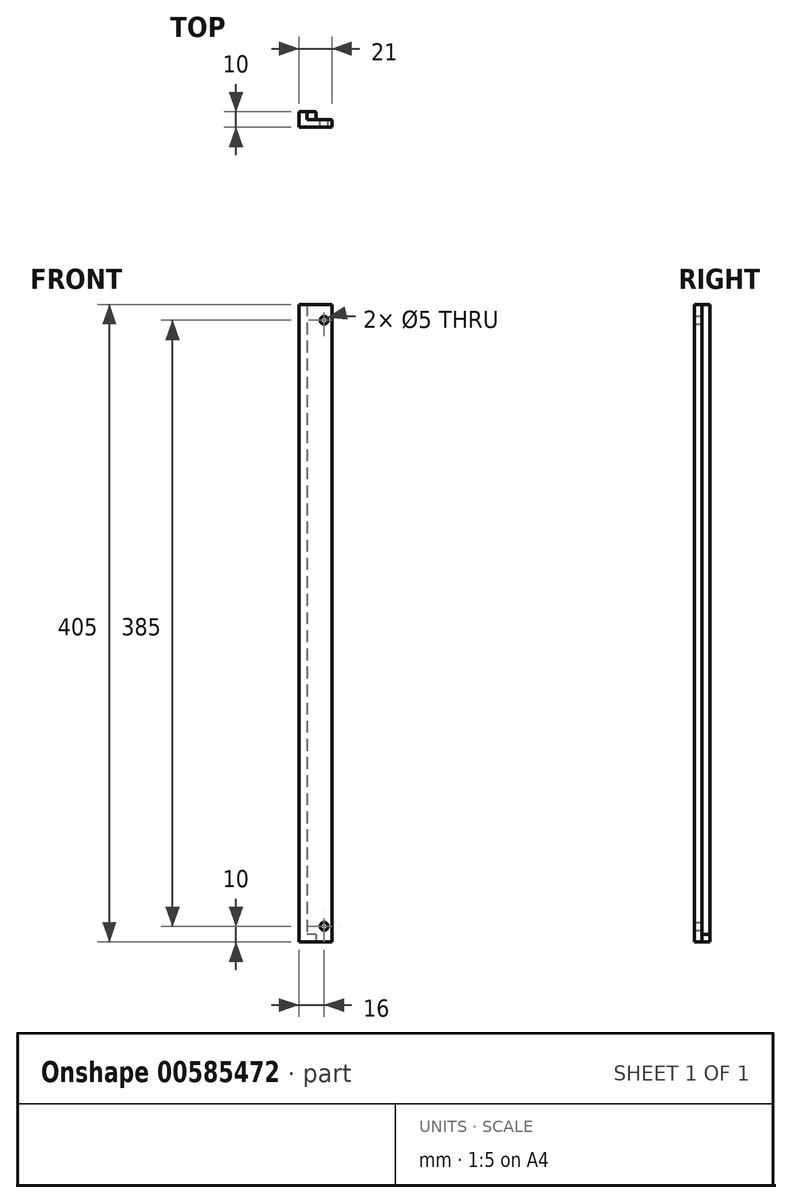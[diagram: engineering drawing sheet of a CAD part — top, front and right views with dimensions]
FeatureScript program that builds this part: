
annotation { "Feature Type Name" : "Feature", "Feature Type Description" : "" }
export const myFeature = defineFeature(function(context is Context, id is Id, definition is map)
    precondition{}
    {
        {
            var Q0;
            Q0=qCreatedBy(makeId("Top.planeOp"),FACE);
            var sketch = newSketch(context, id + "F0", { "sketchPlane" : qUnion([Q0])});
            skLineSegment(sketch, "E0", {"start": v(0, 0) * mm, "end": v(0, -10) * mm});
            skLineSegment(sketch, "E1", {"start": v(0, -10) * mm, "end": v(21, -10) * mm});
            skLineSegment(sketch, "E2", {"start": v(21, -10) * mm, "end": v(21, -5) * mm});
            skLineSegment(sketch, "E3", {"start": v(21, -5) * mm, "end": v(11, -5) * mm});
            skLineSegment(sketch, "E4", {"start": v(11, -5) * mm, "end": v(11, 0) * mm});
            skLineSegment(sketch, "E5", {"start": v(11, 0) * mm, "end": v(6, 0) * mm});
            skLineSegment(sketch, "E6", {"start": v(5, 0) * mm, "end": v(0, 0) * mm});
            skLineSegment(sketch, "E7", {"start": v(5, 0) * mm, "end": v(6, 0) * mm});
            skSolve(sketch);
        }
        {
            var Q0;
            Q0=makeQuery(id+"F0.imprint","IMPRINT",FACE,{"disambiguationData":[TD([[makeQuery(id+"F0.imprint","IMPRINT",EDGE,{"derivedFrom":sQuery(id+"F0.wireOp",EDGE,"E0")}),1.0]])]});
            extrude(context, id + "F1", {"entities" : qUnion([Q0]), "depth" : 5 * mm, "offsetDistance" : 25 * mm});
        }
        {
            var Q0;
            Q0=makeQuery(id+"F1.opExtrude","CAP_FACE",FACE,{"disambiguationData":[OSD([sQuery(id+"F0.wireOp",EDGE,"E0"),sQuery(id+"F0.wireOp",EDGE,"E1"),sQuery(id+"F0.wireOp",EDGE,"E2"),sQuery(id+"F0.wireOp",EDGE,"E3"),sQuery(id+"F0.wireOp",EDGE,"E4"),sQuery(id+"F0.wireOp",EDGE,"E5"),sQuery(id+"F0.wireOp",EDGE,"E6"),sQuery(id+"F0.wireOp",EDGE,"E7")])],"isStart":false});
            var sketch = newSketch(context, id + "F2", { "sketchPlane" : qUnion([Q0])});
            skLineSegment(sketch, "E8", {"start": v(0, 0) * mm, "end": v(0, -10) * mm});
            skLineSegment(sketch, "E9", {"start": v(0, -10) * mm, "end": v(21, -10) * mm});
            skLineSegment(sketch, "E10", {"start": v(21, -10) * mm, "end": v(21, -5) * mm});
            skLineSegment(sketch, "E11", {"start": v(21, -5) * mm, "end": v(11, -5) * mm});
            skLineSegment(sketch, "E12", {"start": v(11, -5) * mm, "end": v(11, 0) * mm});
            skLineSegment(sketch, "E13", {"start": v(11, 0) * mm, "end": v(6, 0) * mm});
            skLineSegment(sketch, "E14", {"start": v(6, 0) * mm, "end": v(6, -5) * mm});
            skLineSegment(sketch, "E15", {"start": v(6, -5) * mm, "end": v(5, -5) * mm});
            skLineSegment(sketch, "E16", {"start": v(5, -5) * mm, "end": v(5, 0) * mm});
            skLineSegment(sketch, "E17", {"start": v(5, 0) * mm, "end": v(0, 0) * mm});
            skSolve(sketch);
        }
        {
            var Q0;
            Q0=makeQuery(id+"F2.imprint","IMPRINT",FACE,{"disambiguationData":[TD([[makeQuery(id+"F2.imprint","IMPRINT",EDGE,{"derivedFrom":sQuery(id+"F2.wireOp",EDGE,"E8")}),1.0]])]});
            extrude(context, id + "F3", {"entities" : qUnion([Q0]), "operationType" : NewBodyOperationType.ADD, "depth" : 400 * mm, "offsetDistance" : 25 * mm});
        }
        {
            var Q0;
            Q0=makeQuery(id+"F3.boolean.opBoolean","MERGE",FACE,{"derivedFrom":[makeQuery(id+"F1.opExtrude","SWEPT_FACE",FACE,{"disambiguationData":[OSD([sQuery(id+"F0.wireOp",EDGE,"E3")])]}),makeQuery(id+"F3.opExtrude","SWEPT_FACE",FACE,{"disambiguationData":[OSD([sQuery(id+"F2.wireOp",EDGE,"E11")])]})]});
            var sketch = newSketch(context, id + "F4", { "sketchPlane" : qUnion([Q0])});
            skLineSegment(sketch, "E18", {"start": v(-16, 0) * mm, "end": v(-16, 10) * mm});
            skSolve(sketch);
        }
        {
            var Q0;
            Q0=sQuery(id+"F4.wireOp",VERTEX,"E18.end");
            var Q1;
            Q1=makeQuery(id+"F1.opExtrude","SWEPT_BODY",BODY,{"disambiguationData":[OSD([sQuery(id+"F0.wireOp",EDGE,"E0"),sQuery(id+"F0.wireOp",EDGE,"E1"),sQuery(id+"F0.wireOp",EDGE,"E2"),sQuery(id+"F0.wireOp",EDGE,"E3"),sQuery(id+"F0.wireOp",EDGE,"E4"),sQuery(id+"F0.wireOp",EDGE,"E5"),sQuery(id+"F0.wireOp",EDGE,"E6"),sQuery(id+"F0.wireOp",EDGE,"E7")])]});
            hole(context, id + "F5", {"style" : HoleStyle.SIMPLE, "endStyle" : HoleEndStyle.THROUGH, "holeDiameter" : 5 * mm, "majorDiameter" : 5 * mm, "isTappedThrough" : true, "tappedDepth" : 12 * mm, "tapClearance" : 3, "locations" : qUnion([Q0]), "scope" : qUnion([Q1])});
        }
        {
            var Q0;
            Q0=makeQuery(id+"F3.boolean.opBoolean","MERGE",FACE,{"derivedFrom":[makeQuery(id+"F1.opExtrude","SWEPT_FACE",FACE,{"disambiguationData":[OSD([sQuery(id+"F0.wireOp",EDGE,"E3")])]}),makeQuery(id+"F3.opExtrude","SWEPT_FACE",FACE,{"disambiguationData":[OSD([sQuery(id+"F2.wireOp",EDGE,"E11")])]})]});
            var sketch = newSketch(context, id + "F6", { "sketchPlane" : qUnion([Q0])});
            skLineSegment(sketch, "E19", {"start": v(-16, 405) * mm, "end": v(-16, 395) * mm});
            skPoint(sketch, "E19.endSnap0", {"position": v(-16, 405) * mm});
            skSolve(sketch);
        }
        {
            var Q0;
            Q0=sQuery(id+"F6.wireOp",VERTEX,"E19.end");
            var Q1;
            Q1=makeQuery(id+"F1.opExtrude","SWEPT_BODY",BODY,{"disambiguationData":[OSD([sQuery(id+"F0.wireOp",EDGE,"E0"),sQuery(id+"F0.wireOp",EDGE,"E1"),sQuery(id+"F0.wireOp",EDGE,"E2"),sQuery(id+"F0.wireOp",EDGE,"E3"),sQuery(id+"F0.wireOp",EDGE,"E4"),sQuery(id+"F0.wireOp",EDGE,"E5"),sQuery(id+"F0.wireOp",EDGE,"E6"),sQuery(id+"F0.wireOp",EDGE,"E7")])]});
            hole(context, id + "F7", {"style" : HoleStyle.SIMPLE, "endStyle" : HoleEndStyle.THROUGH, "holeDiameter" : 5 * mm, "majorDiameter" : 5 * mm, "isTappedThrough" : true, "tappedDepth" : 12 * mm, "tapClearance" : 3, "locations" : qUnion([Q0]), "scope" : qUnion([Q1])});
        }
        {
            var Q0;
            Q0=makeQuery(id+"F3.opExtrude","CAP_FACE",FACE,{"disambiguationData":[OSD([sQuery(id+"F2.wireOp",EDGE,"E8"),sQuery(id+"F2.wireOp",EDGE,"E9"),sQuery(id+"F2.wireOp",EDGE,"E10"),sQuery(id+"F2.wireOp",EDGE,"E11"),sQuery(id+"F2.wireOp",EDGE,"E12"),sQuery(id+"F2.wireOp",EDGE,"E13"),sQuery(id+"F2.wireOp",EDGE,"E14"),sQuery(id+"F2.wireOp",EDGE,"E15"),sQuery(id+"F2.wireOp",EDGE,"E16"),sQuery(id+"F2.wireOp",EDGE,"E17")])],"isStart":false});
            var sketch = newSketch(context, id + "F8", { "sketchPlane" : qUnion([Q0])});
            skLineSegment(sketch, "E20.bottom", {"start": v(6, 0) * mm, "end": v(11, 0) * mm});
            skLineSegment(sketch, "E20.top", {"start": v(6, -5) * mm, "end": v(11, -5) * mm});
            skLineSegment(sketch, "E20.left", {"start": v(6, 0) * mm, "end": v(6, -5) * mm});
            skLineSegment(sketch, "E20.right", {"start": v(11, 0) * mm, "end": v(11, -5) * mm});
            skSolve(sketch);
        }
        {
            var Q0;
            Q0 = qSketchRegion(id + "F8", true);
            extrude(context, id + "F9", {"entities" : qUnion([Q0]), "operationType" : NewBodyOperationType.REMOVE, "oppositeDirection" : true, "depth" : 400 * mm, "offsetDistance" : 25 * mm});
        }
    });
